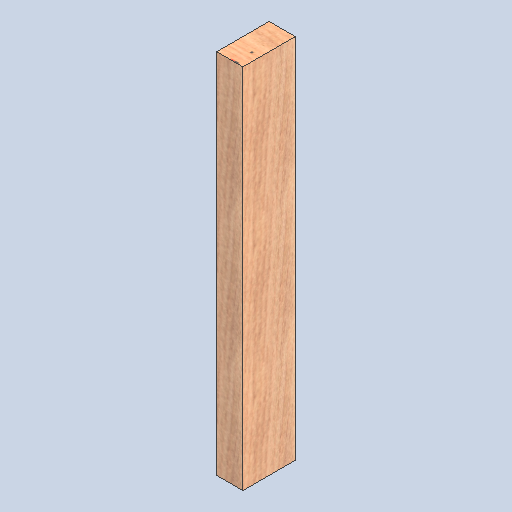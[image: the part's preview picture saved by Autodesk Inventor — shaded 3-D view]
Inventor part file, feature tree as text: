
AUTODESK INVENTOR PART (.ipt)
format: ipt  version: 2025 (Build 290162000, 162)  size: 167,424 bytes
history: native  units: in
note: dims shown in document units (in); Inventor stores cm internally (conversion verified against a paired STEP export)
features: other x3, sketch x1
ambient origin geometry x8: Origin, YZ Plane, XZ Plane, XY Plane, X Axis, Y Axis, Z Axis, Center Point
bodies: Solid1 (feature_tree)
feature tree (4):
  other  "2x4x28.ipt"
  other  "Solid1::2x4x28.ipt"
  other  "TaggingFeature1"
  sketch  "Sketch1"  dims[d0=0.3937in]
